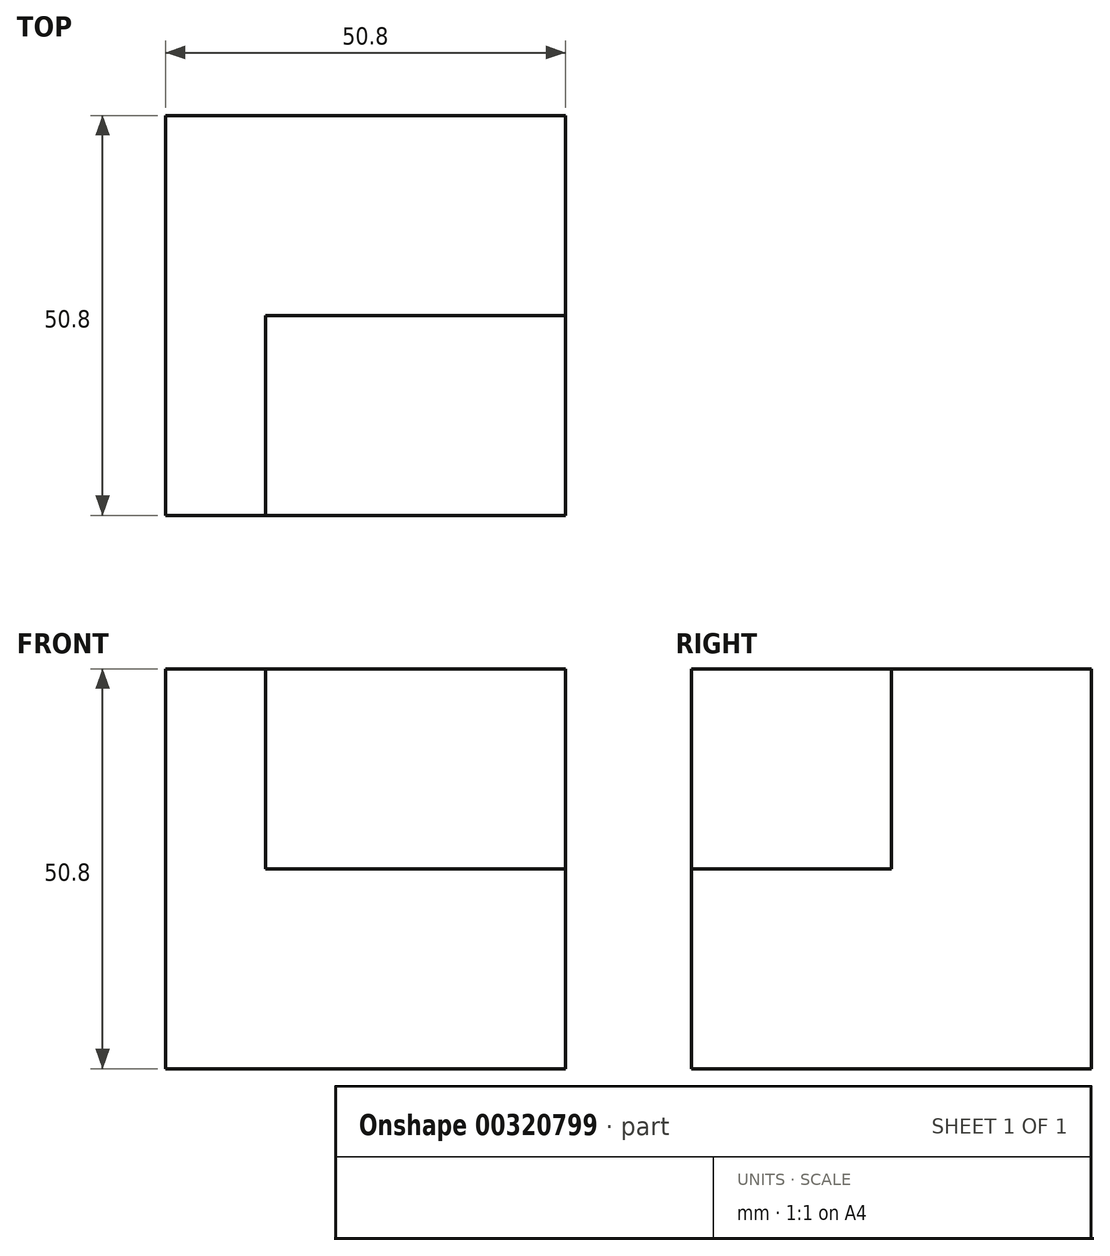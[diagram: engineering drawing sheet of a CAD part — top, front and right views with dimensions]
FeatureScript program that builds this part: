
annotation { "Feature Type Name" : "Feature", "Feature Type Description" : "" }
export const myFeature = defineFeature(function(context is Context, id is Id, definition is map)
    precondition{}
    {
        {
            var Q0;
            Q0=qCreatedBy(makeId("Front.planeOp"),FACE);
            var sketch = newSketch(context, id + "F0", { "sketchPlane" : qUnion([Q0])});
            skLineSegment(sketch, "E0", {"start": v(-28.65, 25.04) * mm, "end": v(-28.65, -25.76) * mm});
            skLineSegment(sketch, "E1", {"start": v(-28.65, -25.76) * mm, "end": v(22.15, -25.76) * mm});
            skLineSegment(sketch, "E2", {"start": v(22.15, -25.76) * mm, "end": v(22.15, 25.04) * mm});
            skLineSegment(sketch, "E3", {"start": v(22.15, 25.04) * mm, "end": v(-28.65, 25.04) * mm});
            skSolve(sketch);
        }
        {
            var Q0;
            Q0=makeQuery(id+"F0.imprint","IMPRINT",FACE,{"disambiguationData":[TD([[makeQuery(id+"F0.imprint","IMPRINT",EDGE,{"derivedFrom":sQuery(id+"F0.wireOp",EDGE,"E0")}),1.0]])]});
            extrude(context, id + "F1", {"entities" : qUnion([Q0]), "depth" : 50.8 * mm});
        }
        {
            var Q0;
            Q0=makeQuery(id+"F1.opExtrude","CAP_FACE",FACE,{"disambiguationData":[OSD([sQuery(id+"F0.wireOp",EDGE,"E0"),sQuery(id+"F0.wireOp",EDGE,"E1"),sQuery(id+"F0.wireOp",EDGE,"E2"),sQuery(id+"F0.wireOp",EDGE,"E3")])],"isStart":false});
            var sketch = newSketch(context, id + "F2", { "sketchPlane" : qUnion([Q0])});
            skLineSegment(sketch, "E4", {"start": v(-15.95, 25.04) * mm, "end": v(-15.95, -0.36) * mm});
            skLineSegment(sketch, "E5", {"start": v(-15.95, -0.36) * mm, "end": v(22.15, -0.36) * mm});
            skLineSegment(sketch, "E6", {"start": v(22.15, -0.36) * mm, "end": v(22.15, 25.04) * mm});
            skLineSegment(sketch, "E7", {"start": v(22.15, 25.04) * mm, "end": v(-15.95, 25.04) * mm});
            skLineSegment(sketch, "E8", {"start": v(-15.95, 12.34) * mm, "end": v(-28.65, 12.34) * mm});
            skSolve(sketch);
        }
        {
            var Q0;
            {var subQ0=sQuery(id+"F2.wireOp",EDGE,"E5");Q0=makeQuery(id+"F2.imprint","IMPRINT",FACE,{"disambiguationData":[TD([[makeQuery(id+"F2.imprint","IMPRINT",EDGE,{"derivedFrom":subQ0}),1.0]])]});}
            extrude(context, id + "F3", {"entities" : qUnion([Q0]), "operationType" : NewBodyOperationType.REMOVE, "oppositeDirection" : true, "depth" : 25.4 * mm});
        }
    });
